# Revit family: Haworth_Masters_AttachedStorage-Sliding Door
name_source: partatom
category: Furniture Systems
revit_build: Autodesk Revit 2018 (Build: 20170223_1515(x64)
units: mm (PartAtom-declared; Revit-internal decimal feet)

## family parameters
Always vertical = Yes
Cut with Voids When Loaded = No
OmniClass Number = 23.40.70.14.64.21
OmniClass Title = Systems Furniture
Part Type = Normal
Room Calculation Point = No
Round Connector Dimension = Use Diameter
Shared = No
Work Plane-Based = No

## types (88) — shared parameters
Assembly Code = E2020200
Custom Size = No
Description = Haworth Masters Attached Storage
Door 1 = Yes
Hardware Finish = Haworth _ Metal _ Brushed Aluminum
Manufacturer = Haworth
Max. Height = 63 1/2"
Max. Width = 108"
Min. Height = 27 1/2"
Min. Width = 29 7/8"
Model = Haworth Masters - Attached Storage -
Revision Number = 1
Size = Verify Final Dim. w/ Haworth
Standard Depths = 18, 23 in.
Standard Widths = 48, 54, 60, 66, 72, 78, 84, 90, 96, 102, 108 in.
Sustainability Info = http://media.haworth.com
URL = http://www.haworth.com
URL - Product = http://www.haworth.com
Warranty = http://www.haworth.com

## per-type parameters (varying)
| type | Actual Depth | Actual Height | Actual Width | Back Cavity | Cabinet Depth | Depth | Door 2 | Door Width | Finished Back | One and One Half High | Top Drawer Height | Two High | Width | With Convergent Worktop |
| 18d 48w - 1.5H Attached Storage - No Back | 18" | 21 5/8" | 47 7/8" | 0" | 18" | 18" | No | 23 7/8" | No | Yes | 6 1/4" | No | 48" | No |
| 18d 54w - 1.5H Attached Storage - No Back | 18" | 21 5/8" | 53 7/8" | 0" | 18" | 18" | No | 26 7/8" | No | Yes | 6 1/4" | No | 54" | No |
| 18d 60w - 1.5H Attached Storage - No Back | 18" | 21 5/8" | 59 7/8" | 0" | 18" | 18" | No | 29 7/8" | No | Yes | 6 1/4" | No | 60" | No |
| 18d 66w - 1.5H Attached Storage - No Back | 18" | 21 5/8" | 65 7/8" | 0" | 18" | 18" | No | 32 7/8" | No | Yes | 6 1/4" | No | 66" | No |
| 18d 72w - 1.5H Attached Storage - No Back | 18" | 21 5/8" | 71 7/8" | 0" | 18" | 18" | No | 35 7/8" | No | Yes | 6 1/4" | No | 72" | No |
| 18d 78w - 1.5H Attached Storage - No Back | 18" | 21 5/8" | 77 7/8" | 0" | 18" | 18" | Yes | 25 229/256" | No | Yes | 6 1/4" | No | 78" | No |
| 18d 84w - 1.5H Attached Storage - No Back | 18" | 21 5/8" | 83 7/8" | 0" | 18" | 18" | Yes | 27 229/256" | No | Yes | 6 1/4" | No | 84" | No |
| 18d 90w - 1.5H Attached Storage - No Back | 18" | 21 5/8" | 89 7/8" | 0" | 18" | 18" | Yes | 29 229/256" | No | Yes | 6 1/4" | No | 90" | No |
| 18d 96w - 1.5H Attached Storage - No Back | 18" | 21 5/8" | 95 7/8" | 0" | 18" | 18" | Yes | 31 229/256" | No | Yes | 6 1/4" | No | 96" | No |
| 18d 102w - 1.5H Attached Storage - No Back | 18" | 21 5/8" | 101 7/8" | 0" | 18" | 18" | Yes | 33 229/256" | No | Yes | 6 1/4" | No | 102" | No |
| 18d 108w - 1.5H Attached Storage - No Back | 18" | 21 5/8" | 107 7/8" | 0" | 18" | 18" | Yes | 35 229/256" | No | Yes | 6 1/4" | No | 108" | No |
| 18d 48w - 1.5H Attached Storage - Finished Back | 18 3/4" | 21 5/8" | 47 7/8" | 0" | 18" | 18" | No | 23 7/8" | Yes | Yes | 6 1/4" | No | 48" | No |
| 18d 54w - 1.5H Attached Storage - Finished Back | 18 3/4" | 21 5/8" | 53 7/8" | 0" | 18" | 18" | No | 26 7/8" | Yes | Yes | 6 1/4" | No | 54" | No |
| 18d 60w - 1.5H Attached Storage - Finished Back | 18 3/4" | 21 5/8" | 59 7/8" | 0" | 18" | 18" | No | 29 7/8" | Yes | Yes | 6 1/4" | No | 60" | No |
| 18d 66w - 1.5H Attached Storage - Finished Back | 18 3/4" | 21 5/8" | 65 7/8" | 0" | 18" | 18" | No | 32 7/8" | Yes | Yes | 6 1/4" | No | 66" | No |
| 18d 72w - 1.5H Attached Storage - Finished Back | 18 3/4" | 21 5/8" | 71 7/8" | 0" | 18" | 18" | No | 35 7/8" | Yes | Yes | 6 1/4" | No | 72" | No |
| 18d 78w - 1.5H Attached Storage - Finished Back | 18 3/4" | 21 5/8" | 77 7/8" | 0" | 18" | 18" | Yes | 25 229/256" | Yes | Yes | 6 1/4" | No | 78" | No |
| 18d 84w - 1.5H Attached Storage - Finished Back | 18 3/4" | 21 5/8" | 83 7/8" | 0" | 18" | 18" | Yes | 27 229/256" | Yes | Yes | 6 1/4" | No | 84" | No |
| 18d 90w - 1.5H Attached Storage - Finished Back | 18 3/4" | 21 5/8" | 89 7/8" | 0" | 18" | 18" | Yes | 29 229/256" | Yes | Yes | 6 1/4" | No | 90" | No |
| 18d 96w - 1.5H Attached Storage - Finished Back | 18 3/4" | 21 5/8" | 95 7/8" | 0" | 18" | 18" | Yes | 31 229/256" | Yes | Yes | 6 1/4" | No | 96" | No |
| 18d 102w - 1.5H Attached Storage - Finished Back | 18 3/4" | 21 5/8" | 101 7/8" | 0" | 18" | 18" | Yes | 33 229/256" | Yes | Yes | 6 1/4" | No | 102" | No |
| 18d 108w - 1.5H Attached Storage - Finished Back | 18 3/4" | 21 5/8" | 107 7/8" | 0" | 18" | 18" | Yes | 35 229/256" | Yes | Yes | 6 1/4" | No | 108" | No |
| 23d 48w - 1.5H Attached Storage for Convergent Worktop - No Back | 23" | 21 5/8" | 47 7/8" | 5" | 23" | 23" | No | 23 7/8" | No | Yes | 6 1/4" | No | 48" | Yes |
| 23d 54w - 1.5H Attached Storage for Convergent Worktop - No Back | 23" | 21 5/8" | 53 7/8" | 5" | 23" | 23" | No | 26 7/8" | No | Yes | 6 1/4" | No | 54" | Yes |
| 23d 60w - 1.5H Attached Storage for Convergent Worktop - No Back | 23" | 21 5/8" | 59 7/8" | 5" | 23" | 23" | No | 29 7/8" | No | Yes | 6 1/4" | No | 60" | Yes |
| 23d 66w - 1.5H Attached Storage for Convergent Worktop - No Back | 23" | 21 5/8" | 65 7/8" | 5" | 23" | 23" | No | 32 7/8" | No | Yes | 6 1/4" | No | 66" | Yes |
| 23d 72w - 1.5H Attached Storage for Convergent Worktop - No Back | 23" | 21 5/8" | 71 7/8" | 5" | 23" | 23" | No | 35 7/8" | No | Yes | 6 1/4" | No | 72" | Yes |
| 23d 78w - 1.5H Attached Storage for Convergent Worktop - No Back | 23" | 21 5/8" | 77 7/8" | 5" | 23" | 23" | Yes | 25 229/256" | No | Yes | 6 1/4" | No | 78" | Yes |
| 23d 84w - 1.5H Attached Storage for Convergent Worktop - No Back | 23" | 21 5/8" | 83 7/8" | 5" | 23" | 23" | Yes | 27 229/256" | No | Yes | 6 1/4" | No | 84" | Yes |
| 23d 90w - 1.5H Attached Storage for Convergent Worktop - No Back | 23" | 21 5/8" | 89 7/8" | 5" | 23" | 23" | Yes | 29 229/256" | No | Yes | 6 1/4" | No | 90" | Yes |
| 23d 96w - 1.5H Attached Storage for Convergent Worktop - No Back | 23" | 21 5/8" | 95 7/8" | 5" | 23" | 23" | Yes | 31 229/256" | No | Yes | 6 1/4" | No | 96" | Yes |
| 23d 102w - 1.5H Attached Storage for Convergent Worktop - No Back | 23" | 21 5/8" | 101 7/8" | 5" | 23" | 23" | Yes | 33 229/256" | No | Yes | 6 1/4" | No | 102" | Yes |
| 23d 108w - 1.5H Attached Storage for Convergent Worktop - No Back | 23" | 21 5/8" | 107 7/8" | 5" | 23" | 23" | Yes | 35 229/256" | No | Yes | 6 1/4" | No | 108" | Yes |
| 23d 48w - 1.5H Attached Storage for Convergent Worktop - Finished Back | 23 3/4" | 21 5/8" | 47 7/8" | 5" | 23" | 23" | No | 23 7/8" | Yes | Yes | 6 1/4" | No | 48" | Yes |
| 23d 54w - 1.5H Attached Storage for Convergent Worktop - Finished Back | 23 3/4" | 21 5/8" | 53 7/8" | 5" | 23" | 23" | No | 26 7/8" | Yes | Yes | 6 1/4" | No | 54" | Yes |
| 23d 60w - 1.5H Attached Storage for Convergent Worktop - Finished Back | 23 3/4" | 21 5/8" | 59 7/8" | 5" | 23" | 23" | No | 29 7/8" | Yes | Yes | 6 1/4" | No | 60" | Yes |
| 23d 66w - 1.5H Attached Storage for Convergent Worktop - Finished Back | 23 3/4" | 21 5/8" | 65 7/8" | 5" | 23" | 23" | No | 32 7/8" | Yes | Yes | 6 1/4" | No | 66" | Yes |
| 23d 72w - 1.5H Attached Storage for Convergent Worktop - Finished Back | 23 3/4" | 21 5/8" | 71 7/8" | 5" | 23" | 23" | No | 35 7/8" | Yes | Yes | 6 1/4" | No | 72" | Yes |
| 23d 78w - 1.5H Attached Storage for Convergent Worktop - Finished Back | 23 3/4" | 21 5/8" | 77 7/8" | 5" | 23" | 23" | Yes | 25 229/256" | Yes | Yes | 6 1/4" | No | 78" | Yes |
| 23d 84w - 1.5H Attached Storage for Convergent Worktop - Finished Back | 23 3/4" | 21 5/8" | 83 7/8" | 5" | 23" | 23" | Yes | 27 229/256" | Yes | Yes | 6 1/4" | No | 84" | Yes |
| 23d 90w - 1.5H Attached Storage for Convergent Worktop - Finished Back | 23 3/4" | 21 5/8" | 89 7/8" | 5" | 23" | 23" | Yes | 29 229/256" | Yes | Yes | 6 1/4" | No | 90" | Yes |
| 23d 96w - 1.5H Attached Storage for Convergent Worktop - Finished Back | 23 3/4" | 21 5/8" | 95 7/8" | 5" | 23" | 23" | Yes | 31 229/256" | Yes | Yes | 6 1/4" | No | 96" | Yes |
| 23d 102w - 1.5H Attached Storage for Convergent Worktop - Finished Back | 23 3/4" | 21 5/8" | 101 7/8" | 5" | 23" | 23" | Yes | 33 229/256" | Yes | Yes | 6 1/4" | No | 102" | Yes |
| 23d 108w - 1.5H Attached Storage for Convergent Worktop - Finished Back | 23 3/4" | 21 5/8" | 107 7/8" | 5" | 23" | 23" | Yes | 35 229/256" | Yes | Yes | 6 1/4" | No | 108" | Yes |
| 18d 48w - 2H Attached Storage - No Back | 18" | 28" | 47 7/8" | 0" | 18" | 18" | No | 23 7/8" | No | No | 13" | Yes | 48" | No |
| 18d 54w - 2H Attached Storage - No Back | 18" | 28" | 53 7/8" | 0" | 18" | 18" | No | 26 7/8" | No | No | 13" | Yes | 54" | No |
| 18d 60w - 2H Attached Storage - No Back | 18" | 28" | 59 7/8" | 0" | 18" | 18" | No | 29 7/8" | No | No | 13" | Yes | 60" | No |
| 18d 66w - 2H Attached Storage - No Back | 18" | 28" | 65 7/8" | 0" | 18" | 18" | No | 32 7/8" | No | No | 13" | Yes | 66" | No |
| 18d 72w - 2H Attached Storage - No Back | 18" | 28" | 71 7/8" | 0" | 18" | 18" | No | 35 7/8" | No | No | 13" | Yes | 72" | No |
| 18d 78w - 2H Attached Storage - No Back | 18" | 28" | 77 7/8" | 0" | 18" | 18" | Yes | 25 229/256" | No | No | 13" | Yes | 78" | No |
| 18d 84w - 2H Attached Storage - No Back | 18" | 28" | 83 7/8" | 0" | 18" | 18" | Yes | 27 229/256" | No | No | 13" | Yes | 84" | No |
| 18d 90w - 2H Attached Storage - No Back | 18" | 28" | 89 7/8" | 0" | 18" | 18" | Yes | 29 229/256" | No | No | 13" | Yes | 90" | No |
| 18d 96w - 2H Attached Storage - No Back | 18" | 28" | 95 7/8" | 0" | 18" | 18" | Yes | 31 229/256" | No | No | 13" | Yes | 96" | No |
| 18d 102w - 2H Attached Storage - No Back | 18" | 28" | 101 7/8" | 0" | 18" | 18" | Yes | 33 229/256" | No | No | 13" | Yes | 102" | No |
| 18d 108w - 2H Attached Storage - No Back | 18" | 28" | 107 7/8" | 0" | 18" | 18" | Yes | 35 229/256" | No | No | 13" | Yes | 108" | No |
| 18d 48w - 2H Attached Storage - Finished Back | 18 3/4" | 28" | 47 7/8" | 0" | 18" | 18" | No | 23 7/8" | Yes | No | 13" | Yes | 48" | No |
| 18d 54w - 2H Attached Storage - Finished Back | 18 3/4" | 28" | 53 7/8" | 0" | 18" | 18" | No | 26 7/8" | Yes | No | 13" | Yes | 54" | No |
| 18d 60w - 2H Attached Storage - Finished Back | 18 3/4" | 28" | 59 7/8" | 0" | 18" | 18" | No | 29 7/8" | Yes | No | 13" | Yes | 60" | No |
| 18d 66w - 2H Attached Storage - Finished Back | 18 3/4" | 28" | 65 7/8" | 0" | 18" | 18" | No | 32 7/8" | Yes | No | 13" | Yes | 66" | No |
| 18d 72w - 2H Attached Storage - Finished Back | 18 3/4" | 28" | 71 7/8" | 0" | 18" | 18" | No | 35 7/8" | Yes | No | 13" | Yes | 72" | No |
| 18d 78w - 2H Attached Storage - Finished Back | 18 3/4" | 28" | 77 7/8" | 0" | 18" | 18" | Yes | 25 229/256" | Yes | No | 13" | Yes | 78" | No |
| 18d 84w - 2H Attached Storage - Finished Back | 18 3/4" | 28" | 83 7/8" | 0" | 18" | 18" | Yes | 27 229/256" | Yes | No | 13" | Yes | 84" | No |
| 18d 90w - 2H Attached Storage - Finished Back | 18 3/4" | 28" | 89 7/8" | 0" | 18" | 18" | Yes | 29 229/256" | Yes | No | 13" | Yes | 90" | No |
| 18d 96w - 2H Attached Storage - Finished Back | 18 3/4" | 28" | 95 7/8" | 0" | 18" | 18" | Yes | 31 229/256" | Yes | No | 13" | Yes | 96" | No |
| 18d 102w - 2H Attached Storage - Finished Back | 18 3/4" | 28" | 101 7/8" | 0" | 18" | 18" | Yes | 33 229/256" | Yes | No | 13" | Yes | 102" | No |
| 18d 108w - 2H Attached Storage - Finished Back | 18 3/4" | 28" | 107 7/8" | 0" | 18" | 18" | Yes | 35 229/256" | Yes | No | 13" | Yes | 108" | No |
| 23d 48w - 2H Attached Storage for Convergent Worktop - No Back | 23" | 28" | 47 7/8" | 5" | 23" | 23" | No | 23 7/8" | No | No | 13" | Yes | 48" | Yes |
| 23d 54w - 2H Attached Storage for Convergent Worktop - No Back | 23" | 28" | 53 7/8" | 5" | 23" | 23" | No | 26 7/8" | No | No | 13" | Yes | 54" | Yes |
| 23d 60w - 2H Attached Storage for Convergent Worktop - No Back | 23" | 28" | 59 7/8" | 5" | 23" | 23" | No | 29 7/8" | No | No | 13" | Yes | 60" | Yes |
| 23d 66w - 2H Attached Storage for Convergent Worktop - No Back | 23" | 28" | 65 7/8" | 5" | 23" | 23" | No | 32 7/8" | No | No | 13" | Yes | 66" | Yes |
| 23d 72w - 2H Attached Storage for Convergent Worktop - No Back | 23" | 28" | 71 7/8" | 5" | 23" | 23" | No | 35 7/8" | No | No | 13" | Yes | 72" | Yes |
| 23d 78w - 2H Attached Storage for Convergent Worktop - No Back | 23" | 28" | 77 7/8" | 5" | 23" | 23" | Yes | 25 229/256" | No | No | 13" | Yes | 78" | Yes |
| 23d 84w - 2H Attached Storage for Convergent Worktop - No Back | 23" | 28" | 83 7/8" | 5" | 23" | 23" | Yes | 27 229/256" | No | No | 13" | Yes | 84" | Yes |
| 23d 90w - 2H Attached Storage for Convergent Worktop - No Back | 23" | 28" | 89 7/8" | 5" | 23" | 23" | Yes | 29 229/256" | No | No | 13" | Yes | 90" | Yes |
| 23d 96w - 2H Attached Storage for Convergent Worktop - No Back | 23" | 28" | 95 7/8" | 5" | 23" | 23" | Yes | 31 229/256" | No | No | 13" | Yes | 96" | Yes |
| 23d 102w - 2H Attached Storage for Convergent Worktop - No Back | 23" | 28" | 101 7/8" | 5" | 23" | 23" | Yes | 33 229/256" | No | No | 13" | Yes | 102" | Yes |
| 23d 108w - 2H Attached Storage for Convergent Worktop - No Back | 23" | 28" | 107 7/8" | 5" | 23" | 23" | Yes | 35 229/256" | No | No | 13" | Yes | 108" | Yes |
| 23d 48w - 2H Attached Storage for Convergent Worktop - Finished Back | 23 3/4" | 28" | 47 7/8" | 5" | 23" | 23" | No | 23 7/8" | Yes | No | 13" | Yes | 48" | Yes |
| 23d 54w - 2H Attached Storage for Convergent Worktop - Finished Back | 23 3/4" | 28" | 53 7/8" | 5" | 23" | 23" | No | 26 7/8" | Yes | No | 13" | Yes | 54" | Yes |
| 23d 60w - 2H Attached Storage for Convergent Worktop - Finished Back | 23 3/4" | 28" | 59 7/8" | 5" | 23" | 23" | No | 29 7/8" | Yes | No | 13" | Yes | 60" | Yes |
| 23d 66w - 2H Attached Storage for Convergent Worktop - Finished Back | 23 3/4" | 28" | 65 7/8" | 5" | 23" | 23" | No | 32 7/8" | Yes | No | 13" | Yes | 66" | Yes |
| 23d 72w - 2H Attached Storage for Convergent Worktop - Finished Back | 23 3/4" | 28" | 71 7/8" | 5" | 23" | 23" | No | 35 7/8" | Yes | No | 13" | Yes | 72" | Yes |
| 23d 78w - 2H Attached Storage for Convergent Worktop - Finished Back | 23 3/4" | 28" | 77 7/8" | 5" | 23" | 23" | Yes | 25 229/256" | Yes | No | 13" | Yes | 78" | Yes |
| 23d 84w - 2H Attached Storage for Convergent Worktop - Finished Back | 23 3/4" | 28" | 83 7/8" | 5" | 23" | 23" | Yes | 27 229/256" | Yes | No | 13" | Yes | 84" | Yes |
| 23d 90w - 2H Attached Storage for Convergent Worktop - Finished Back | 23 3/4" | 28" | 89 7/8" | 5" | 23" | 23" | Yes | 29 229/256" | Yes | No | 13" | Yes | 90" | Yes |
| 23d 96w - 2H Attached Storage for Convergent Worktop - Finished Back | 23 3/4" | 28" | 95 7/8" | 5" | 23" | 23" | Yes | 31 229/256" | Yes | No | 13" | Yes | 96" | Yes |
| 23d 102w - 2H Attached Storage for Convergent Worktop - Finished Back | 23 3/4" | 28" | 101 7/8" | 5" | 23" | 23" | Yes | 33 229/256" | Yes | No | 13" | Yes | 102" | Yes |
| 23d 108w - 2H Attached Storage for Convergent Worktop - Finished Back | 23 3/4" | 28" | 107 7/8" | 5" | 23" | 23" | Yes | 35 229/256" | Yes | No | 13" | Yes | 108" | Yes |
